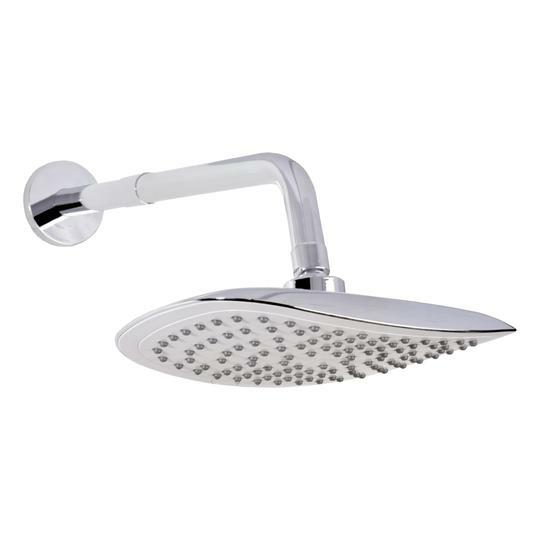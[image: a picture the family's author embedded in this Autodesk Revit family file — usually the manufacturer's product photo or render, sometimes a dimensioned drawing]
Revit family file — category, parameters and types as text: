
# Revit family: 01-2844-11 CONJUNTO REGISTRO DUCHA PRISTINA
name_source: partatom
category: Plumbing Fixtures
revit_build: Autodesk Revit 2018 (Build: 20170223_1515(x64)
units: mm (PartAtom-declared; Revit-internal decimal feet)

## family parameters
Cut with Voids When Loaded = No
Host = Face
OmniClass Number = 23.31.11.00
Part Type = Normal
Room Calculation Point = No
Round Connector Dimension = Use Diameter
Shared = No

## types (1)
- 01-2844-11
    Ancho manija = 75 mm
    CW Connection = Yes
    Default Elevation = 0 mm  [stored 0 ft]
    Description = Mezclador ducha
    Escudo = 60 mm  [stored 0.19685 ft]
    HW Connection = Yes
    Laton = Laton
    Link Ficha Tecnica = No encontrada en internet
    Manufacturer = Gricol
    Metal Laton Cromado = Metal Laton Cromado
    Model = 01-2844-11
    Plastico ABS Cromado = Plastico ABS Cromado
    Product Name = CONJUNTO REGISTRO DUCHA PRISTINA
    Sepacion entre registro y ducha = 400 mm  [stored 1.31234 ft]
    Type Image = <None>
    URL = https://www.gricol.com
    Vent Connection = No
    Waste Connection = No

note: [stored X ft] marks values corroborated as IEEE doubles in the binary element streams (Revit-internal decimal feet)

## geometry (parser evidence)
native form markers: Blend x4, Sweep x14
no freeform markers — native parametric forms only
